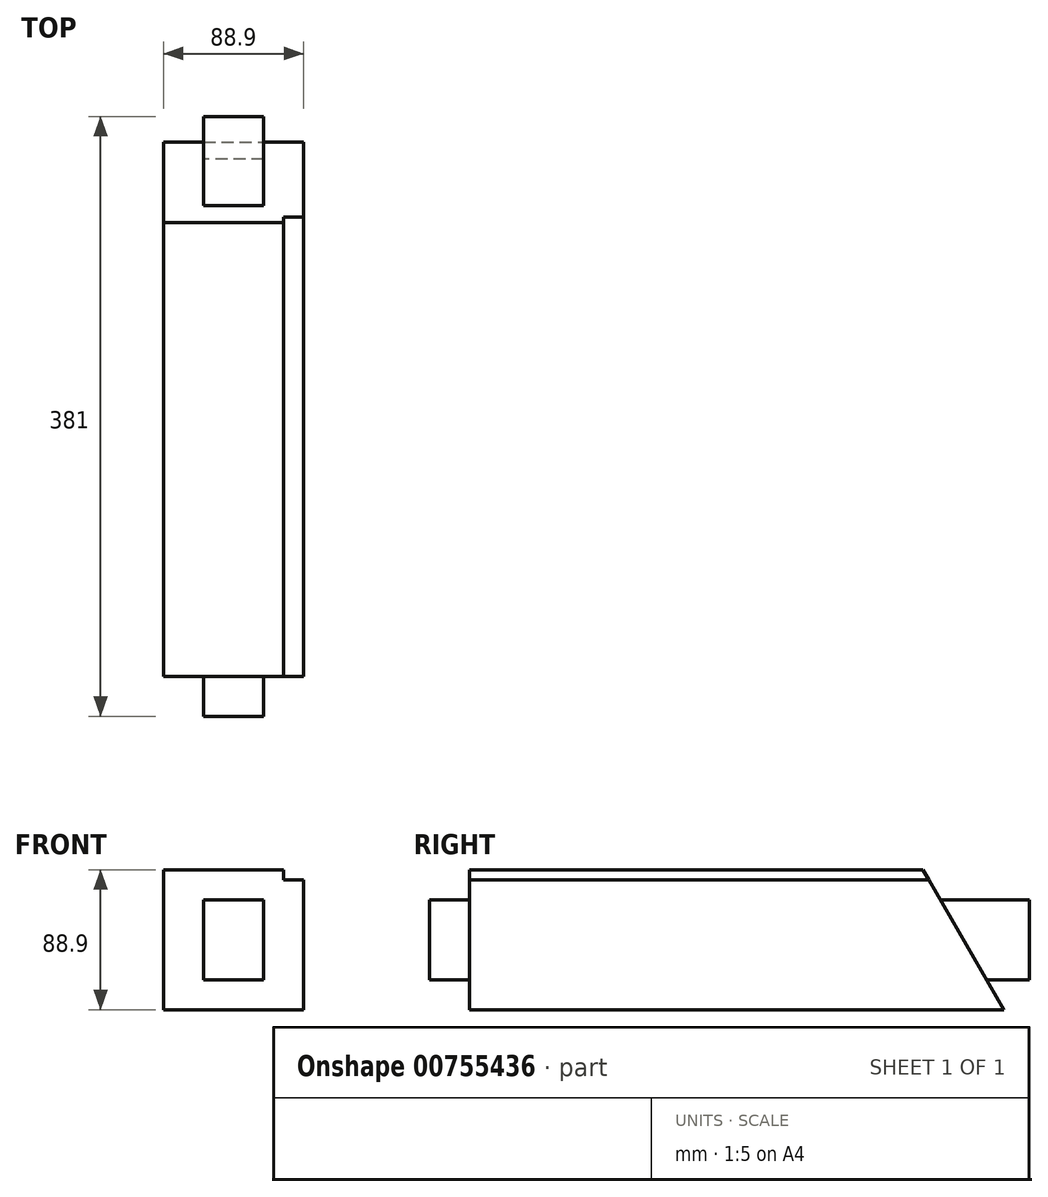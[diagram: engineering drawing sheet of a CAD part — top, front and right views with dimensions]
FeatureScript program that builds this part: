
annotation { "Feature Type Name" : "Feature", "Feature Type Description" : "" }
export const myFeature = defineFeature(function(context is Context, id is Id, definition is map)
    precondition{}
    {
        {
            var Q0;
            Q0=qCreatedBy(makeId("Right.planeOp"),FACE);
            var sketch = newSketch(context, id + "F0", { "sketchPlane" : qUnion([Q0])});
            skLineSegment(sketch, "E0.bottom", {"start": v(-190.5, 44.45) * mm, "end": v(190.5, 44.45) * mm});
            skLineSegment(sketch, "E0.top", {"start": v(-190.5, -44.45) * mm, "end": v(190.5, -44.45) * mm});
            skLineSegment(sketch, "E0.left", {"start": v(-190.5, 44.45) * mm, "end": v(-190.5, -44.45) * mm});
            skLineSegment(sketch, "E0.right", {"start": v(190.5, 44.45) * mm, "end": v(190.5, -44.45) * mm});
            skPoint(sketch, "E0.middle", {"position": v(0, 0) * mm});
            skSolve(sketch);
        }
        {
            var Q0;
            Q0 = qSketchRegion(id + "F0", true);
            extrude(context, id + "F1", {"entities" : qUnion([Q0]), "endBound" : BoundingType.SYMMETRIC, "depth" : 88.9 * mm, "offsetDistance" : 25.4 * mm});
        }
        {
            var Q0;
            Q0=makeQuery(id+"F1.opExtrude","SWEPT_FACE",FACE,{"disambiguationData":[OSD([sQuery(id+"F0.wireOp",EDGE,"E0.bottom")])]});
            var sketch = newSketch(context, id + "F2", { "sketchPlane" : qUnion([Q0])});
            skLineSegment(sketch, "E1", {"start": v(-44.45, 122.94) * mm, "end": v(44.45, 122.94) * mm});
            skSolve(sketch);
        }
        {
            var Q0;
            Q0=sQuery(id+"F2.wireOp",EDGE,"E1");
            cPlane(context, id + "F3", {"entities" : qUnion([Q0]), "cplaneType" : CPlaneType.LINE_ANGLE, "offset" : 25.4 * mm, "angle" : 30 * degree, "width" : 152.4 * mm, "height" : 152.4 * mm});
        }
        {
            var Q0;
            Q0=makeQuery(id+"F1.opExtrude","SWEPT_FACE",FACE,{"disambiguationData":[OSD([sQuery(id+"F0.wireOp",EDGE,"E0.right")])]});
            var sketch = newSketch(context, id + "F4", { "sketchPlane" : qUnion([Q0])});
            skLineSegment(sketch, "E2.bottom", {"start": v(-44.45, 44.45) * mm, "end": v(-31.75, 44.45) * mm});
            skLineSegment(sketch, "E2.top", {"start": v(-44.45, 38.1) * mm, "end": v(-31.75, 38.1) * mm});
            skLineSegment(sketch, "E2.left", {"start": v(-44.45, 44.45) * mm, "end": v(-44.45, 38.1) * mm});
            skLineSegment(sketch, "E2.right", {"start": v(-31.75, 44.45) * mm, "end": v(-31.75, 38.1) * mm});
            skSolve(sketch);
        }
        {
            var Q0;
            Q0 = qSketchRegion(id + "F4", true);
            extrude(context, id + "F5", {"entities" : qUnion([Q0]), "operationType" : NewBodyOperationType.REMOVE, "endBound" : BoundingType.THROUGH_ALL, "oppositeDirection" : true, "depth" : 25.4 * mm, "offsetDistance" : 25.4 * mm});
        }
        {
            var Q0;
            Q0=makeQuery(id+"F1.opExtrude","SWEPT_FACE",FACE,{"disambiguationData":[OSD([sQuery(id+"F0.wireOp",EDGE,"E0.right")])]});
            var sketch = newSketch(context, id + "F6", { "sketchPlane" : qUnion([Q0])});
            skLineSegment(sketch, "E3.bottom", {"start": v(44.45, 44.45) * mm, "end": v(-44.45, 44.45) * mm});
            skLineSegment(sketch, "E3.top", {"start": v(44.45, -44.45) * mm, "end": v(-44.45, -44.45) * mm});
            skLineSegment(sketch, "E3.left", {"start": v(44.45, 44.45) * mm, "end": v(44.45, -44.45) * mm});
            skLineSegment(sketch, "E3.right", {"start": v(-44.45, 44.45) * mm, "end": v(-44.45, -44.45) * mm});
            skPoint(sketch, "E3.middle", {"position": v(0, 0) * mm});
            skLineSegment(sketch, "E4.bottom", {"start": v(19.05, 25.4) * mm, "end": v(-19.05, 25.4) * mm});
            skLineSegment(sketch, "E4.top", {"start": v(19.05, -25.4) * mm, "end": v(-19.05, -25.4) * mm});
            skLineSegment(sketch, "E4.left", {"start": v(19.05, 25.4) * mm, "end": v(19.05, -25.4) * mm});
            skLineSegment(sketch, "E4.right", {"start": v(-19.05, 25.4) * mm, "end": v(-19.05, -25.4) * mm});
            skSolve(sketch);
        }
        {
            var Q0;
            Q0 = qSketchRegion(id + "F6", true);
            var Q1;
            Q1=qCreatedBy(id+"F3.planeOp",FACE);
            extrude(context, id + "F7", {"entities" : qUnion([Q0]), "operationType" : NewBodyOperationType.REMOVE, "endBound" : BoundingType.UP_TO_SURFACE, "oppositeDirection" : true, "depth" : 25.4 * mm, "endBoundEntityFace" : qUnion([Q1]), "offsetDistance" : 25.4 * mm});
        }
        {
            var Q0;
            Q0=makeQuery(id+"F1.opExtrude","SWEPT_FACE",FACE,{"disambiguationData":[OSD([sQuery(id+"F0.wireOp",EDGE,"E0.left")])]});
            var sketch = newSketch(context, id + "F8", { "sketchPlane" : qUnion([Q0])});
            skLineSegment(sketch, "E5.bottom", {"start": v(-44.45, 44.45) * mm, "end": v(44.45, 44.45) * mm});
            skLineSegment(sketch, "E5.top", {"start": v(-44.45, -44.45) * mm, "end": v(44.45, -44.45) * mm});
            skLineSegment(sketch, "E5.left", {"start": v(-44.45, 44.45) * mm, "end": v(-44.45, -44.45) * mm});
            skLineSegment(sketch, "E5.right", {"start": v(44.45, 44.45) * mm, "end": v(44.45, -44.45) * mm});
            skPoint(sketch, "E5.middle", {"position": v(0, 0) * mm});
            skLineSegment(sketch, "E6.bottom", {"start": v(-19.05, 25.4) * mm, "end": v(19.05, 25.4) * mm});
            skLineSegment(sketch, "E6.top", {"start": v(-19.05, -25.4) * mm, "end": v(19.05, -25.4) * mm});
            skLineSegment(sketch, "E6.left", {"start": v(-19.05, 25.4) * mm, "end": v(-19.05, -25.4) * mm});
            skLineSegment(sketch, "E6.right", {"start": v(19.05, 25.4) * mm, "end": v(19.05, -25.4) * mm});
            skSolve(sketch);
        }
        {
            var Q0;
            Q0 = qSketchRegion(id + "F8", true);
            extrude(context, id + "F9", {"entities" : qUnion([Q0]), "operationType" : NewBodyOperationType.REMOVE, "oppositeDirection" : true, "depth" : 25.4 * mm, "offsetDistance" : 25.4 * mm});
        }
    });
